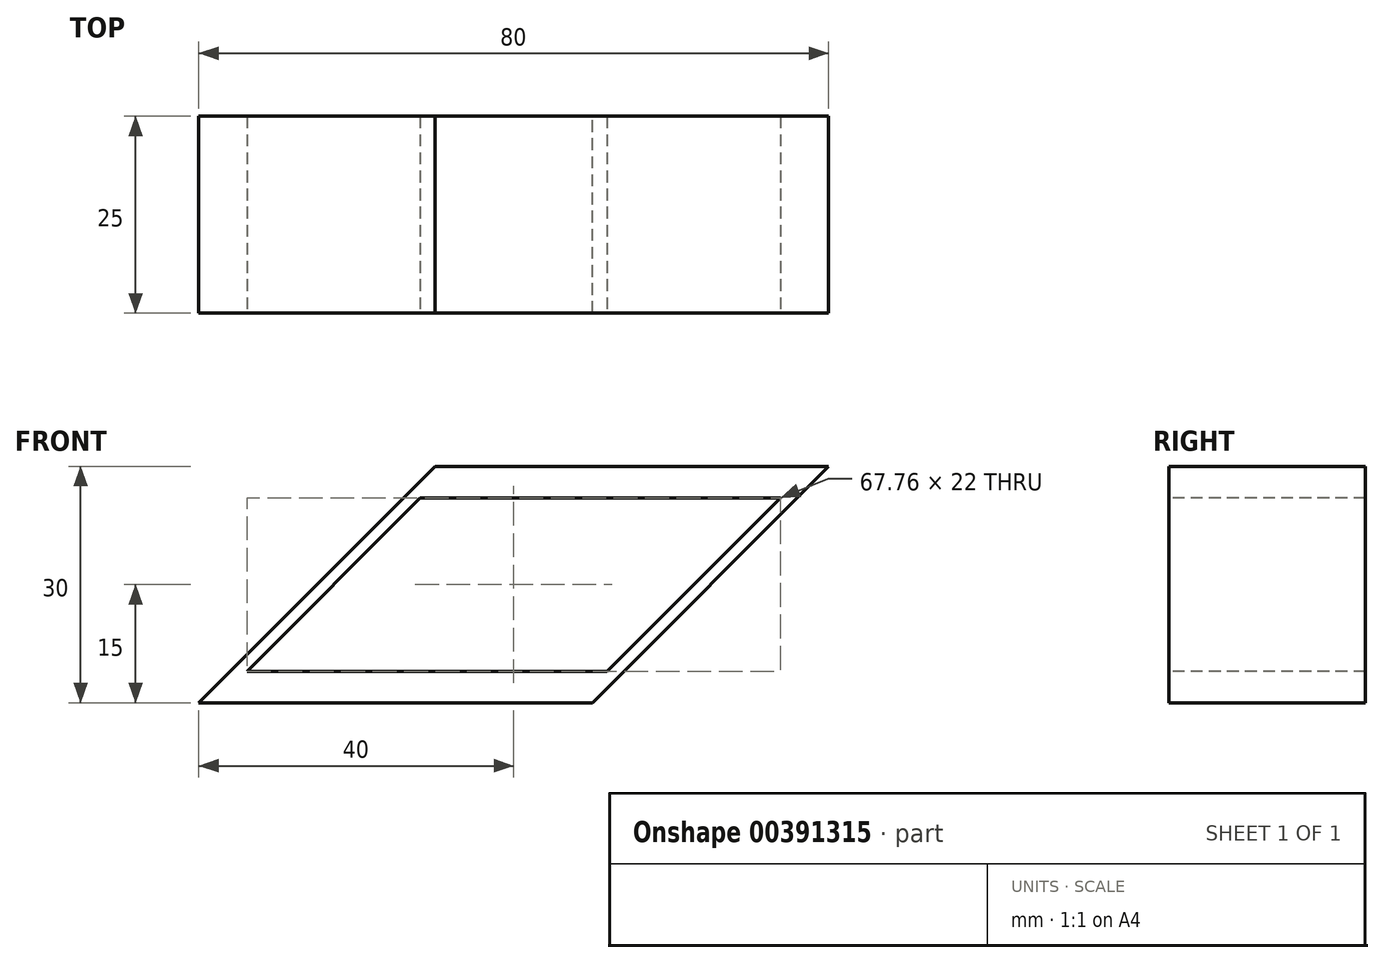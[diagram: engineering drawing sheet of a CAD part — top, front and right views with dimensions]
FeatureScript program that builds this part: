
annotation { "Feature Type Name" : "Feature", "Feature Type Description" : "" }
export const myFeature = defineFeature(function(context is Context, id is Id, definition is map)
    precondition{}
    {
        {
            var Q0;
            Q0=qCreatedBy(makeId("Front.planeOp"),FACE);
            var sketch = newSketch(context, id + "F0", { "sketchPlane" : qUnion([Q0])});
            skLineSegment(sketch, "E0", {"start": v(0, 0) * mm, "end": v(50, 0) * mm});
            skLineSegment(sketch, "E1", {"start": v(50, 0) * mm, "end": v(80, 30) * mm});
            skLineSegment(sketch, "E2", {"start": v(80, 30) * mm, "end": v(30, 30) * mm});
            skLineSegment(sketch, "E3", {"start": v(30, 30) * mm, "end": v(0, 0) * mm});
            skSolve(sketch);
        }
        {
            var Q0;
            Q0=makeQuery(id+"F0.imprint","IMPRINT",FACE,{"disambiguationData":[TD([[makeQuery(id+"F0.imprint","IMPRINT",EDGE,{"derivedFrom":sQuery(id+"F0.wireOp",EDGE,"E0")}),1.0]])]});
            extrude(context, id + "F1", {"entities" : qUnion([Q0]), "depth" : 25 * mm, "offsetDistance" : 25 * mm});
        }
        {
            var Q0;
            Q0=makeQuery(id+"F1.opExtrude","CAP_FACE",FACE,{"disambiguationData":[OSD([sQuery(id+"F0.wireOp",EDGE,"E0"),sQuery(id+"F0.wireOp",EDGE,"E1"),sQuery(id+"F0.wireOp",EDGE,"E2"),sQuery(id+"F0.wireOp",EDGE,"E3")])],"isStart":false});
            var sketch = newSketch(context, id + "F2", { "sketchPlane" : qUnion([Q0])});
            skLineSegment(sketch, "E4", {"start": v(28.12, 26) * mm, "end": v(73.88, 26) * mm});
            skLineSegment(sketch, "E5", {"start": v(73.88, 26) * mm, "end": v(51.88, 4) * mm});
            skLineSegment(sketch, "E6", {"start": v(51.88, 4) * mm, "end": v(6.12, 4) * mm});
            skLineSegment(sketch, "E7", {"start": v(6.12, 4) * mm, "end": v(28.12, 26) * mm});
            skSolve(sketch);
        }
        {
            var Q0;
            Q0 = qSketchRegion(id + "F2", true);
            extrude(context, id + "F3", {"entities" : qUnion([Q0]), "operationType" : NewBodyOperationType.REMOVE, "endBound" : BoundingType.THROUGH_ALL, "oppositeDirection" : true, "depth" : 25 * mm, "offsetDistance" : 25 * mm});
        }
    });
